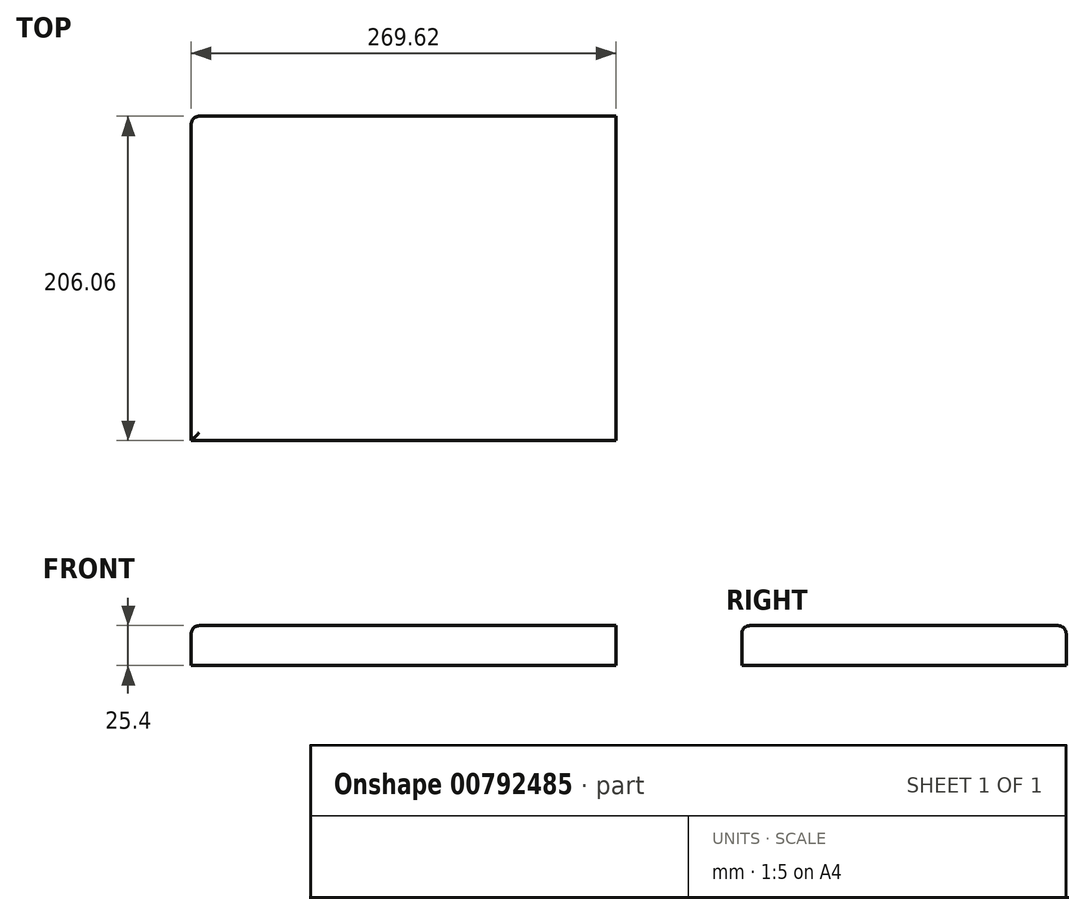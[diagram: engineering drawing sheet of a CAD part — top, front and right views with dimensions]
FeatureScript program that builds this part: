
annotation { "Feature Type Name" : "Feature", "Feature Type Description" : "" }
export const myFeature = defineFeature(function(context is Context, id is Id, definition is map)
    precondition{}
    {
        {
            var Q0;
            Q0=qCreatedBy(makeId("Top.planeOp"),FACE);
            var sketch = newSketch(context, id + "F0", { "sketchPlane" : qUnion([Q0])});
            skLineSegment(sketch, "E0.bottom", {"start": v(-134.8, -103.03) * mm, "end": v(134.8, -103.03) * mm});
            skLineSegment(sketch, "E0.top", {"start": v(-134.8, 103.03) * mm, "end": v(134.8, 103.03) * mm});
            skLineSegment(sketch, "E0.left", {"start": v(-134.8, -103.03) * mm, "end": v(-134.8, 103.03) * mm});
            skLineSegment(sketch, "E0.right", {"start": v(134.8, -103.03) * mm, "end": v(134.8, 103.03) * mm});
            skPoint(sketch, "E0.middle", {"position": v(0, 0) * mm});
            skSolve(sketch);
        }
        {
            var Q0;
            Q0 = qSketchRegion(id + "F0", true);
            extrude(context, id + "F1", {"entities" : qUnion([Q0]), "depth" : 25.4 * mm, "offsetDistance" : 25.4 * mm});
        }
        {
            var Q0;
            Q0=makeQuery(id+"F1.opExtrude","CAP_EDGE",EDGE,{"disambiguationData":[OSD([sQuery(id+"F0.wireOp",EDGE,"E0.left")])],"isStart":false});
            var Q1;
            Q1=makeQuery(id+"F1.opExtrude","CAP_EDGE",EDGE,{"disambiguationData":[OSD([sQuery(id+"F0.wireOp",EDGE,"E0.bottom")])],"isStart":false});
            fillet(context, id + "F2", {"entities" : qUnion([Q0, Q1]), "radius" : 5.08 * mm, "tangentPropagation" : true, "allowEdgeOverflow" : false});
        }
        {
            var Q0;
            Q0=makeQuery(id+"F1.opExtrude","CAP_EDGE",EDGE,{"disambiguationData":[OSD([sQuery(id+"F0.wireOp",EDGE,"E0.top")])],"isStart":false});
            fillet(context, id + "F3", {"entities" : qUnion([Q0]), "radius" : 5.08 * mm, "tangentPropagation" : true, "allowEdgeOverflow" : false});
        }
    });
